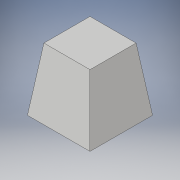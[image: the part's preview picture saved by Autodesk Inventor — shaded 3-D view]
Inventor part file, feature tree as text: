
AUTODESK INVENTOR PART (.ipt)
format: ipt  version: 2019 (Build 230136000, 136)  size: 100,864 bytes
history: native  units: mm
features: extrude x2, sketch x2
ambient origin geometry x8: Origin, YZ Plane, XZ Plane, XY Plane, X Axis, Y Axis, Z Axis, Center Point
bodies: Solid1 (feature_tree)
feature tree (4):
  extrude  "Extrusion1"  Depth=10.0mm
  extrude  "Extrusion2"  Depth=3.0mm
  sketch  "Sketch1"  dims[d0=10.0mm d1=10.0mm]
  sketch  "Sketch2"  dims[d2=10.0mm d3=-1.308997mm d4=4.2mm d5=3.0mm d6=-0.436332mm]
